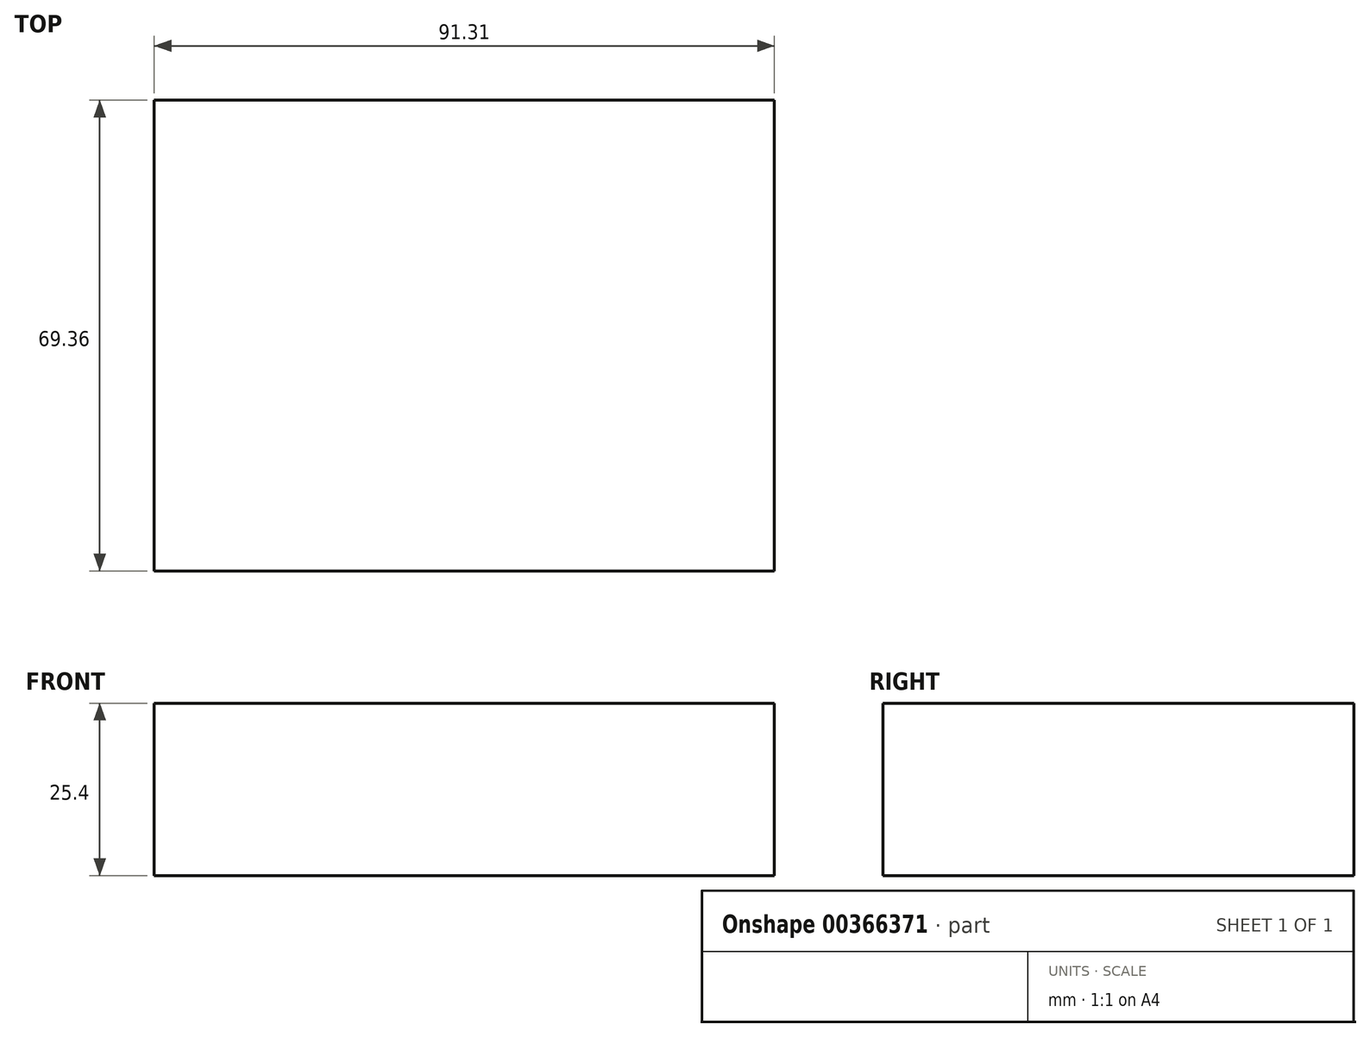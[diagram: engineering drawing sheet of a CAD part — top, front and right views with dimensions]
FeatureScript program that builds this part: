
annotation { "Feature Type Name" : "Feature", "Feature Type Description" : "" }
export const myFeature = defineFeature(function(context is Context, id is Id, definition is map)
    precondition{}
    {
        {
            var Q0;
            Q0=qCreatedBy(makeId("Top.planeOp"),FACE);
            var sketch = newSketch(context, id + "F0", { "sketchPlane" : qUnion([Q0])});
            skLineSegment(sketch, "E0.bottom", {"start": v(-54.14, -35.96) * mm, "end": v(37.17, -35.96) * mm});
            skLineSegment(sketch, "E0.top", {"start": v(-54.14, 33.4) * mm, "end": v(37.17, 33.4) * mm});
            skLineSegment(sketch, "E0.left", {"start": v(-54.14, -35.96) * mm, "end": v(-54.14, 33.4) * mm});
            skLineSegment(sketch, "E0.right", {"start": v(37.17, -35.96) * mm, "end": v(37.17, 33.4) * mm});
            skSolve(sketch);
        }
        {
            var Q0;
            Q0 = qSketchRegion(id + "F0", true);
            extrude(context, id + "F1", {"entities" : qUnion([Q0]), "depth" : 25.4 * mm});
        }
    });
